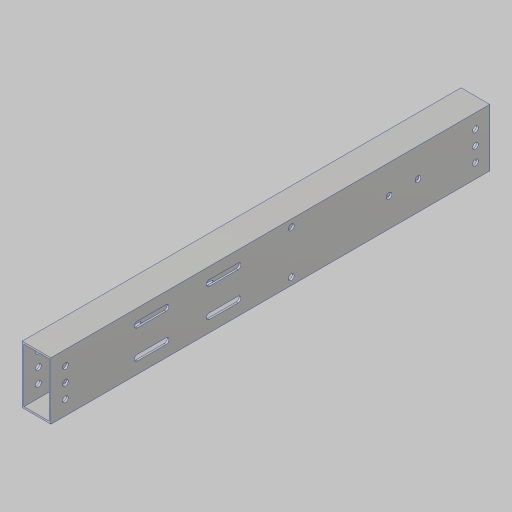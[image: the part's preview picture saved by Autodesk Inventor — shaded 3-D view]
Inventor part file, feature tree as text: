
AUTODESK INVENTOR PART (.ipt)
format: ipt  version: 2023.5 (Build 275446000, 446)  size: 195,072 bytes
history: native  units: in
note: dims shown in document units (in); Inventor stores cm internally (conversion verified against a paired STEP export)
features: sketch x4, hole x3, projected_geometry x3, extrude x2, mirror x1
ambient origin geometry x8: Origin, YZ Plane, XZ Plane, XY Plane, X Axis, Y Axis, Z Axis, Center Point
bodies: Solid1 (feature_tree)
feature tree (13):
  extrude  "Extrusion1"  Depth=0.5in
  hole  "Hole1"  [1 undecoded]
  mirror  "Mirror1"
  hole  "Hole2"  [1 undecoded]
  extrude  "Extrusion2"  Depth=0.201in
  hole  "Hole3"  [1 undecoded]
  sketch  "Sketch2"  dims[d4=0.0in d5=0.5in]
  sketch  "Sketch3"  dims[d6=0.5in d7=0.5in]
  sketch  "Sketch4"  dims[d8=0.201in d9=0.75in d10=0.385in d11=0.25in d12=0.5635in d13=1.0in d14=0.8108in d15=2.0in]
  sketch  "Sketch5"  dims[d16=1.0in d17=0.201in d18=0.38in d19=0.385in d20=0.25in d21=0.5635in d22=1.0in d23=0.8108in d25=0.201in d26=1.0in d27=1.0in d28=6.0in d29=0.201in d30=1.0in d31=1.0in d32=2.5in d33=0.0in d34=0.0in d35=1.5in d36=1.75in d37=0.201in d38=0.75in d39=0.385in d40=0.25in d41=0.5635in d42=1.0in d43=0.8108in]
  projected_geometry  "Project Cut Edges1"
  projected_geometry  "Project Cut Edges2"
  projected_geometry  "Project Cut Edges3"
note: 3 required parameter values undecoded (feature->parameter linkage not recoverable at this tier; creation-order binding heuristic only, values carry confidence <= 0.55)
